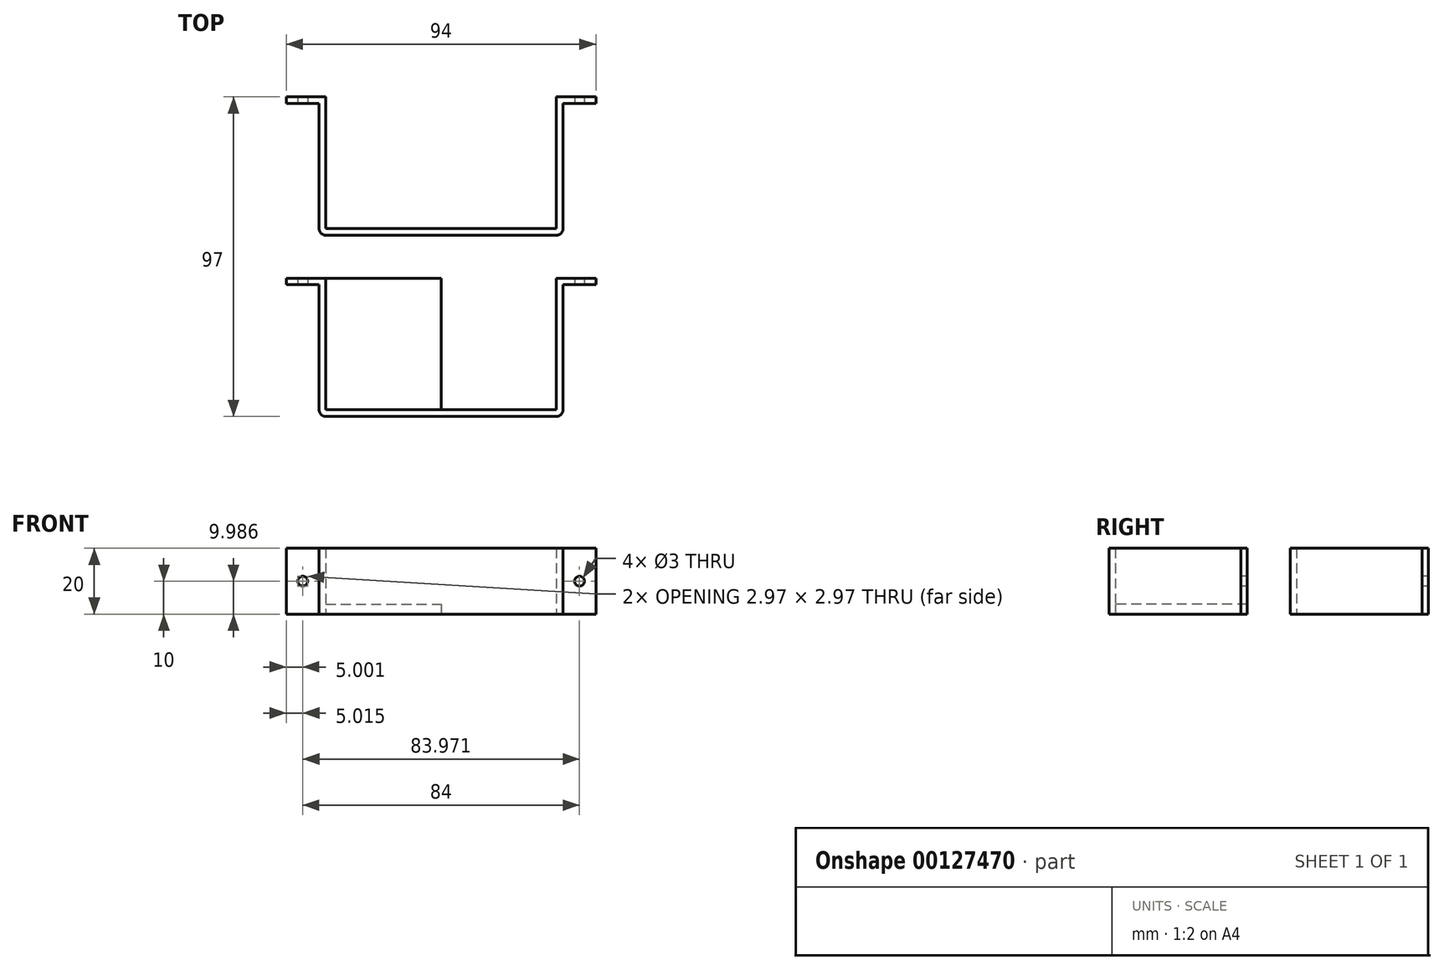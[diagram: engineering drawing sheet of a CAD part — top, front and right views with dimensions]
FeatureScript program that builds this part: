
annotation { "Feature Type Name" : "Feature", "Feature Type Description" : "" }
export const myFeature = defineFeature(function(context is Context, id is Id, definition is map)
    precondition{}
    {
        {
            var Q0;
            Q0=qCreatedBy(makeId("Top.planeOp"),FACE);
            var sketch = newSketch(context, id + "F0", { "sketchPlane" : qUnion([Q0])});
            skLineSegment(sketch, "E0.bottom", {"start": v(-15.96, 8.8) * mm, "end": v(19.04, 8.8) * mm});
            skLineSegment(sketch, "E0.top", {"start": v(-15.96, -31.2) * mm, "end": v(19.04, -31.2) * mm});
            skLineSegment(sketch, "E0.left", {"start": v(-15.96, 8.8) * mm, "end": v(-15.96, -31.2) * mm});
            skLineSegment(sketch, "E0.right", {"start": v(19.04, 8.8) * mm, "end": v(19.04, -31.2) * mm});
            skLineSegment(sketch, "E1", {"start": v(-15.96, 8.8) * mm, "end": v(-27.96, 8.8) * mm});
            skLineSegment(sketch, "E2", {"start": v(-27.96, 8.8) * mm, "end": v(-27.96, 6.8) * mm});
            skLineSegment(sketch, "E3", {"start": v(-27.96, 6.8) * mm, "end": v(-17.96, 6.8) * mm});
            skLineSegment(sketch, "E4", {"start": v(-17.96, 6.8) * mm, "end": v(-17.96, -33.2) * mm});
            skLineSegment(sketch, "E5", {"start": v(-17.96, -33.2) * mm, "end": v(19.04, -33.2) * mm});
            skLineSegment(sketch, "E6", {"start": v(19.04, -33.2) * mm, "end": v(19.04, -31.2) * mm});
            skSolve(sketch);
        }
        {
            var Q0;
            Q0=makeQuery(id+"F0.imprint","IMPRINT",FACE,{"disambiguationData":[TD([[makeQuery(id+"F0.imprint","IMPRINT",EDGE,{"derivedFrom":sQuery(id+"F0.wireOp",EDGE,"E0.top")}),-1.0]])]});
            extrude(context, id + "F1", {"entities" : qUnion([Q0]), "depth" : 20 * mm});
        }
        {
            var Q0;
            Q0=makeQuery(id+"F1.opExtrude","SWEPT_EDGE",EDGE,{"disambiguationData":[OSD([sQuery(id+"F0.wireOp",EDGE,"E4"),sQuery(id+"F0.wireOp",EDGE,"E5")])]});
            fillet(context, id + "F2", {"entities" : qUnion([Q0]), "radius" : 2 * mm, "tangentPropagation" : true, "allowEdgeOverflow" : false});
        }
        {
            var Q0;
            Q0=makeQuery(id+"F1.opExtrude","SWEPT_FACE",FACE,{"disambiguationData":[OSD([sQuery(id+"F0.wireOp",EDGE,"E3")])]});
            var sketch = newSketch(context, id + "F3", { "sketchPlane" : qUnion([Q0])});
            skPoint(sketch, "E7", {"position": v(-22.96, 10) * mm});
            skSolve(sketch);
        }
        {
            var Q0;
            Q0=sQuery(id+"F3.wireOp",VERTEX,"E7");
            var Q1;
            Q1=makeQuery(id+"F1.opExtrude","SWEPT_BODY",BODY,{"disambiguationData":[OSD([sQuery(id+"F0.wireOp",EDGE,"E0.top"),sQuery(id+"F0.wireOp",EDGE,"E0.left"),sQuery(id+"F0.wireOp",EDGE,"E1"),sQuery(id+"F0.wireOp",EDGE,"E2"),sQuery(id+"F0.wireOp",EDGE,"E3"),sQuery(id+"F0.wireOp",EDGE,"E4"),sQuery(id+"F0.wireOp",EDGE,"E5"),sQuery(id+"F0.wireOp",EDGE,"E6")])]});
            hole(context, id + "F4", {"style" : HoleStyle.SIMPLE, "endStyle" : HoleEndStyle.THROUGH, "holeDiameter" : 3 * mm, "locations" : qUnion([Q0]), "scope" : qUnion([Q1]), "isTappedThrough" : true});
        }
        {
            var Q0;
            Q0=makeQuery(id+"F1.opExtrude","SWEPT_BODY",BODY,{"disambiguationData":[OSD([sQuery(id+"F0.wireOp",EDGE,"E0.top"),sQuery(id+"F0.wireOp",EDGE,"E0.left"),sQuery(id+"F0.wireOp",EDGE,"E1"),sQuery(id+"F0.wireOp",EDGE,"E2"),sQuery(id+"F0.wireOp",EDGE,"E3"),sQuery(id+"F0.wireOp",EDGE,"E4"),sQuery(id+"F0.wireOp",EDGE,"E5"),sQuery(id+"F0.wireOp",EDGE,"E6")])]});
            var Q1;
            Q1=makeQuery(id+"F1.opExtrude","SWEPT_FACE",FACE,{"disambiguationData":[OSD([sQuery(id+"F0.wireOp",EDGE,"E6")])]});
            mirror(context, id + "F5", {"operationType" : NewBodyOperationType.ADD, "entities" : qUnion([Q0]), "mirrorPlane" : qUnion([Q1])});
        }
        {
            var Q0;
            Q0=makeQuery(id+"F1.opExtrude","SWEPT_BODY",BODY,{"disambiguationData":[OSD([sQuery(id+"F0.wireOp",EDGE,"E0.top"),sQuery(id+"F0.wireOp",EDGE,"E0.left"),sQuery(id+"F0.wireOp",EDGE,"E1"),sQuery(id+"F0.wireOp",EDGE,"E2"),sQuery(id+"F0.wireOp",EDGE,"E3"),sQuery(id+"F0.wireOp",EDGE,"E4"),sQuery(id+"F0.wireOp",EDGE,"E5"),sQuery(id+"F0.wireOp",EDGE,"E6")])]});
            transform(context, id + "F6", {"entities" : qUnion([Q0]), "transformType" : TransformType.COPY});
        }
        {
            var Q0;
            Q0=makeQuery(id+"F6.opPattern","COPY",BODY,{"derivedFrom":makeQuery(id+"F1.opExtrude","SWEPT_BODY",BODY,{"disambiguationData":[OSD([sQuery(id+"F0.wireOp",EDGE,"E0.top"),sQuery(id+"F0.wireOp",EDGE,"E0.left"),sQuery(id+"F0.wireOp",EDGE,"E1"),sQuery(id+"F0.wireOp",EDGE,"E2"),sQuery(id+"F0.wireOp",EDGE,"E3"),sQuery(id+"F0.wireOp",EDGE,"E4"),sQuery(id+"F0.wireOp",EDGE,"E5"),sQuery(id+"F0.wireOp",EDGE,"E6")])]}),"instanceName":"1"});
            transform(context, id + "F7", {"entities" : qUnion([Q0]), "transformType" : TransformType.TRANSLATION_3D, "dx" : 0 * mm, "dy" : 55 * mm, "dz" : 0 * mm, "makeCopy" : false});
        }
        {
            var Q0;
            Q0 = qSketchRegion(id + "F0", true);
            extrude(context, id + "F8", {"entities" : qUnion([Q0]), "operationType" : NewBodyOperationType.ADD, "depth" : 3 * mm});
        }
        {
            var Q0;
            Q0=makeQuery(id+"F8.opExtrude","SWEPT_EDGE",EDGE,{"disambiguationData":[OSD([sQuery(id+"F0.wireOp",EDGE,"E4"),sQuery(id+"F0.wireOp",EDGE,"E5")])]});
            fillet(context, id + "F9", {"entities" : qUnion([Q0]), "radius" : 2 * mm, "tangentPropagation" : true, "allowEdgeOverflow" : false});
        }
    });
